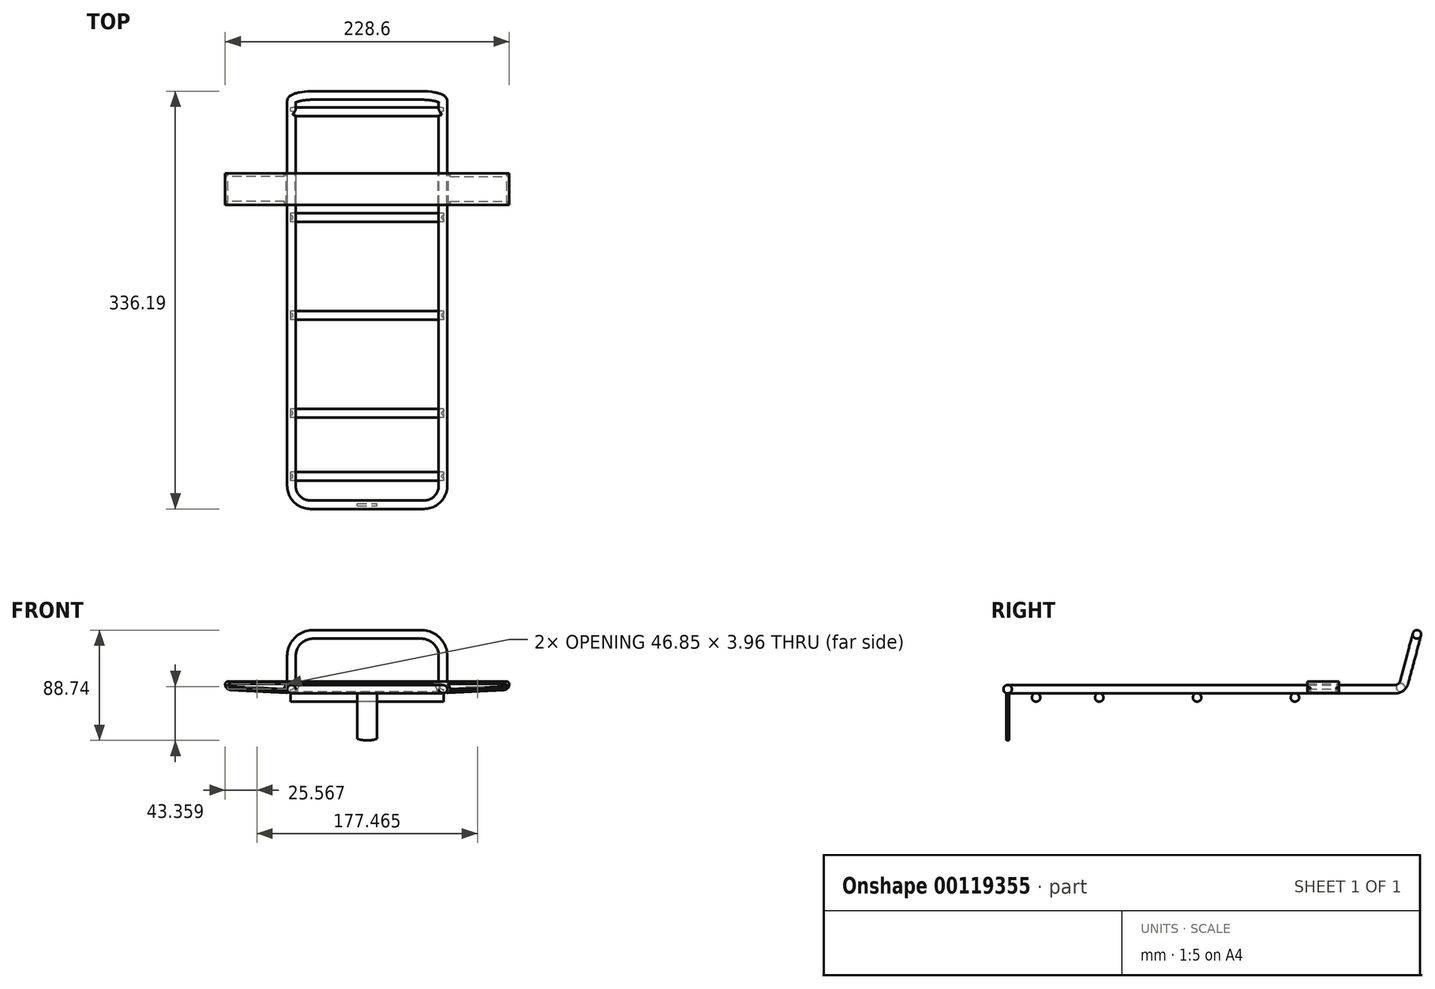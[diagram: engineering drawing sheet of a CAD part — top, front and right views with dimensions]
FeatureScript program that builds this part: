
annotation { "Feature Type Name" : "Feature", "Feature Type Description" : "" }
export const myFeature = defineFeature(function(context is Context, id is Id, definition is map)
    precondition{}
    {
        {
            var Q0;
            Q0=qCreatedBy(makeId("Right.planeOp"),FACE);
            var sketch = newSketch(context, id + "F0", { "sketchPlane" : qUnion([Q0])});
            skCircle(sketch, "E0", {"center": v(0, 0) * mm, "radius": 3.43 * mm});
            skSolve(sketch);
        }
        {
            var Q0;
            Q0=qCreatedBy(makeId("Top.planeOp"),FACE);
            var sketch = newSketch(context, id + "F1", { "sketchPlane" : qUnion([Q0])});
            skLineSegment(sketch, "E1", {"start": v(0, 0) * mm, "end": v(45.72, 0) * mm});
            skArc(sketch, "E2", {"start": v(45.72, 0) * mm, "mid": v(56.5, 4.46) * mm, "end": v(60.96, 15.24) * mm});
            skLineSegment(sketch, "E3", {"start": v(45.72, 0) * mm, "end": v(60.96, 0) * mm, "construction": true});
            skLineSegment(sketch, "E4", {"start": v(60.96, 0) * mm, "end": v(60.96, 15.24) * mm, "construction": true});
            skSolve(sketch);
        }
        {
            var Q0;
            Q0=sQuery(id+"F1.wireOp",EDGE,"E4");
            cPlane(context, id + "F2", {"entities" : qUnion([Q0]), "cplaneType" : CPlaneType.LINE_ANGLE, "offset" : 25.4 * mm, "angle" : 90 * degree, "width" : 152.4 * mm, "height" : 152.4 * mm});
        }
        {
            var Q0;
            Q0=qCreatedBy(id+"F2.planeOp",FACE);
            var sketch = newSketch(context, id + "F3", { "sketchPlane" : qUnion([Q0])});
            skLineSegment(sketch, "E5", {"start": v(15.24, 0) * mm, "end": v(311.65, 0) * mm});
            skArc(sketch, "E6", {"start": v(311.65, 0) * mm, "mid": v(316.3, 1.57) * mm, "end": v(319.01, 5.65) * mm});
            skLineSegment(sketch, "E7", {"start": v(311.65, 0) * mm, "end": v(317.5, 0) * mm, "construction": true});
            skLineSegment(sketch, "E8", {"start": v(317.5, 0) * mm, "end": v(319.01, 5.65) * mm, "construction": true});
            skSolve(sketch);
        }
        {
            var Q0;
            Q0=sQuery(id+"F3.wireOp",EDGE,"E8");
            cPlane(context, id + "F4", {"entities" : qUnion([Q0]), "cplaneType" : CPlaneType.LINE_ANGLE, "offset" : 25.4 * mm, "angle" : 90 * degree, "width" : 152.4 * mm, "height" : 152.4 * mm});
        }
        {
            var Q0;
            Q0=qCreatedBy(id+"F4.planeOp",FACE);
            var sketch = newSketch(context, id + "F5", { "sketchPlane" : qUnion([Q0])});
            skLineSegment(sketch, "E9", {"start": v(-60.96, 88.02) * mm, "end": v(-60.96, 110.12) * mm});
            skArc(sketch, "E10", {"start": v(-43.18, 127.9) * mm, "mid": v(-55.75, 122.69) * mm, "end": v(-60.96, 110.12) * mm});
            skLineSegment(sketch, "E11", {"start": v(-43.18, 127.9) * mm, "end": v(43.18, 127.9) * mm});
            skArc(sketch, "E12", {"start": v(60.96, 110.12) * mm, "mid": v(55.75, 122.69) * mm, "end": v(43.18, 127.9) * mm});
            skLineSegment(sketch, "E13", {"start": v(60.96, 110.12) * mm, "end": v(60.96, 88.02) * mm});
            skLineSegment(sketch, "E14", {"start": v(-60.96, 110.12) * mm, "end": v(-60.96, 127.9) * mm, "construction": true});
            skLineSegment(sketch, "E15", {"start": v(-60.96, 127.9) * mm, "end": v(-43.18, 127.9) * mm, "construction": true});
            skLineSegment(sketch, "E16", {"start": v(43.18, 127.9) * mm, "end": v(60.96, 127.9) * mm, "construction": true});
            skLineSegment(sketch, "E17", {"start": v(60.96, 127.9) * mm, "end": v(60.96, 110.12) * mm, "construction": true});
            skLineSegment(sketch, "E18", {"start": v(-60.96, 88.02) * mm, "end": v(60.96, 88.02) * mm, "construction": true});
            skLineSegment(sketch, "E19", {"start": v(0, 88.02) * mm, "end": v(0, 0) * mm, "construction": true});
            skSolve(sketch);
        }
        {
            var Q0;
            Q0=sQuery(id+"F5.wireOp",EDGE,"E13");
            cPlane(context, id + "F6", {"entities" : qUnion([Q0]), "cplaneType" : CPlaneType.LINE_ANGLE, "offset" : 25.4 * mm, "angle" : 0 * degree, "width" : 152.4 * mm, "height" : 152.4 * mm});
        }
        {
            var Q0;
            Q0=qCreatedBy(id+"F6.planeOp",FACE);
            var sketch = newSketch(context, id + "F7", { "sketchPlane" : qUnion([Q0])});
            skArc(sketch, "E20", {"start": v(-319.01, 5.65) * mm, "mid": v(-316.3, 1.57) * mm, "end": v(-311.65, 0) * mm});
            skLineSegment(sketch, "E21", {"start": v(-311.65, 0) * mm, "end": v(-15.24, 0) * mm});
            skSolve(sketch);
        }
        {
            var Q0;
            Q0=qCreatedBy(makeId("Top.planeOp"),FACE);
            var sketch = newSketch(context, id + "F8", { "sketchPlane" : qUnion([Q0])});
            skArc(sketch, "E22", {"start": v(-60.96, 15.24) * mm, "mid": v(-56.5, 4.46) * mm, "end": v(-45.72, 0) * mm});
            skLineSegment(sketch, "E23", {"start": v(-45.72, 0) * mm, "end": v(0, 0) * mm});
            skSolve(sketch);
        }
        {
            var Q0;
            Q0=qSketchRegion(id+"F0",true);
            var Q1;
            Q1=qConstructionFilter(qBodyType(qCreatedBy(id+"F1",EDGE),BodyType.WIRE),ConstructionObject.NO);
            var Q2;
            Q2=qConstructionFilter(qBodyType(qCreatedBy(id+"F3",EDGE),BodyType.WIRE),ConstructionObject.NO);
            var Q3;
            Q3=qConstructionFilter(qBodyType(qCreatedBy(id+"F5",EDGE),BodyType.WIRE),ConstructionObject.NO);
            var Q4;
            Q4=qConstructionFilter(qBodyType(qCreatedBy(id+"F7",EDGE),BodyType.WIRE),ConstructionObject.NO);
            var Q5;
            Q5=qConstructionFilter(qBodyType(qCreatedBy(id+"F8",EDGE),BodyType.WIRE),ConstructionObject.NO);
            sweep(context, id + "F9", {"profiles" : qUnion([Q0]), "path" : qUnion([Q1, Q2, Q3, Q4, Q5])});
        }
        {
            var Q0;
            Q0=qCreatedBy(makeId("Front.planeOp"),FACE);
            var sketch = newSketch(context, id + "F10", { "sketchPlane" : qUnion([Q0])});
            skLineSegment(sketch, "E24.bottom", {"start": v(-8, 0) * mm, "end": v(8, 0) * mm});
            skLineSegment(sketch, "E24.left", {"start": v(-8, 0) * mm, "end": v(-8, -39.85) * mm});
            skLineSegment(sketch, "E24.right", {"start": v(8, 0) * mm, "end": v(8, -39.85) * mm});
            skArc(sketch, "E25", {"start": v(-8, -39.85) * mm, "mid": v(0, -41.15) * mm, "end": v(8, -39.85) * mm});
            skSolve(sketch);
        }
        {
            var Q0;
            Q0=qSketchRegion(id+"F10",true);
            extrude(context, id + "F11", {"entities" : qUnion([Q0]), "operationType" : NewBodyOperationType.ADD, "endBound" : BoundingType.SYMMETRIC, "depth" : 2.03 * mm});
        }
        {
            var Q0;
            Q0=qCreatedBy(makeId("Right.planeOp"),FACE);
            var sketch = newSketch(context, id + "F12", { "sketchPlane" : qUnion([Q0])});
            skCircle(sketch, "E26", {"center": v(22.86, -6.6) * mm, "radius": 3.43 * mm});
            skCircle(sketch, "E27", {"center": v(73.66, -6.6) * mm, "radius": 3.43 * mm});
            skLineSegment(sketch, "E28", {"start": v(0, -3.18) * mm, "end": v(311.65, -3.18) * mm, "construction": true});
            skCircle(sketch, "E29", {"center": v(152.4, -6.6) * mm, "radius": 3.43 * mm});
            skCircle(sketch, "E30", {"center": v(231.14, -6.6) * mm, "radius": 3.43 * mm});
            skCircle(sketch, "E31", {"center": v(316.23, 1.27) * mm, "radius": 3.43 * mm});
            skSolve(sketch);
        }
        {
            var Q0;
            Q0=qSketchRegion(id+"F12",true);
            extrude(context, id + "F13", {"entities" : qUnion([Q0]), "operationType" : NewBodyOperationType.ADD, "endBound" : BoundingType.SYMMETRIC, "depth" : 123.19 * mm});
        }
        {
            var Q0;
            Q0=qCreatedBy(makeId("Front.planeOp"),FACE);
            cPlane(context, id + "F14", {"entities" : qUnion([Q0]), "cplaneType" : CPlaneType.OFFSET, "offset" : 266.7 * mm, "oppositeDirection" : true, "width" : 152.4 * mm, "height" : 152.4 * mm});
        }
        {
            var Q0;
            Q0=qCreatedBy(id+"F14.planeOp",FACE);
            var sketch = newSketch(context, id + "F15", { "sketchPlane" : qUnion([Q0])});
            skCircle(sketch, "E32", {"center": v(-60.96, 0) * mm, "radius": 3.43 * mm, "construction": true});
            skCircle(sketch, "E33", {"center": v(60.96, 0) * mm, "radius": 3.43 * mm, "construction": true});
            skLineSegment(sketch, "E34", {"start": v(60.96, 3.43) * mm, "end": v(-60.96, 3.43) * mm, "construction": true});
            skArc(sketch, "E35", {"start": v(112.01, 6.22) * mm, "mid": v(113.63, 5.55) * mm, "end": v(114.3, 3.94) * mm});
            skArc(sketch, "E36", {"start": v(114.3, 3.94) * mm, "mid": v(113.04, 0.79) * mm, "end": v(109.96, -0.63) * mm});
            skArc(sketch, "E37", {"start": v(-112.01, 6.22) * mm, "mid": v(-113.63, 5.55) * mm, "end": v(-114.3, 3.94) * mm});
            skArc(sketch, "E38", {"start": v(-114.3, 3.94) * mm, "mid": v(-113.04, 0.79) * mm, "end": v(-109.96, -0.63) * mm});
            skArc(sketch, "E39", {"start": v(64.2, -2.2) * mm, "mid": v(60.96, 3.43) * mm, "end": v(57.72, -2.2) * mm});
            skArc(sketch, "E40", {"start": v(64.2, -2.2) * mm, "mid": v(64.2, -2.71) * mm, "end": v(64.67, -2.95) * mm});
            skArc(sketch, "E41", {"start": v(57.72, -2.2) * mm, "mid": v(57.54, -2.88) * mm, "end": v(56.85, -2.73) * mm});
            skArc(sketch, "E42", {"start": v(-57.72, -2.2) * mm, "mid": v(-60.96, 3.43) * mm, "end": v(-64.2, -2.2) * mm});
            skArc(sketch, "E43", {"start": v(-57.72, -2.2) * mm, "mid": v(-57.54, -2.88) * mm, "end": v(-56.85, -2.73) * mm});
            skLineSegment(sketch, "E44", {"start": v(-109.96, -0.63) * mm, "end": v(-64.67, -2.95) * mm});
            skArc(sketch, "E45", {"start": v(-64.2, -2.2) * mm, "mid": v(-64.2, -2.71) * mm, "end": v(-64.67, -2.95) * mm});
            skLineSegment(sketch, "E46", {"start": v(64.67, -2.95) * mm, "end": v(109.96, -0.63) * mm});
            skLineSegment(sketch, "E47", {"start": v(112.01, 6.22) * mm, "end": v(0, 6.22) * mm});
            skLineSegment(sketch, "E48", {"start": v(0, 6.22) * mm, "end": v(-112.01, 6.22) * mm});
            skLineSegment(sketch, "E49", {"start": v(50.99, 4.2) * mm, "end": v(-50.99, 4.2) * mm});
            skArc(sketch, "E50", {"start": v(-56.85, -2.73) * mm, "mid": v(-56.3, -1.63) * mm, "end": v(-56.05, -0.44) * mm});
            skArc(sketch, "E51", {"start": v(56.05, -0.44) * mm, "mid": v(56.3, -1.63) * mm, "end": v(56.85, -2.73) * mm});
            skArc(sketch, "E52", {"start": v(56.05, -0.44) * mm, "mid": v(54.42, 2.86) * mm, "end": v(50.99, 4.2) * mm});
            skArc(sketch, "E53", {"start": v(-50.99, 4.2) * mm, "mid": v(-54.42, 2.86) * mm, "end": v(-56.05, -0.44) * mm});
            skLineSegment(sketch, "E54", {"start": v(64.64, -2.45) * mm, "end": v(57.28, -2.45) * mm, "construction": true});
            skLineSegment(sketch, "E55", {"start": v(-57.28, -2.45) * mm, "end": v(-64.64, -2.45) * mm, "construction": true});
            skSolve(sketch);
        }
        {
            var Q0;
            Q0=qSketchRegion(id+"F15",true);
            extrude(context, id + "F16", {"entities" : qUnion([Q0]), "depth" : 25.4 * mm});
        }
        {
            var Q0;
            Q0=makeQuery(id+"F16.opExtrude","CAP_FACE",FACE,{"disambiguationData":[OSD([sQuery(id+"F15.wireOp",EDGE,"E35"),sQuery(id+"F15.wireOp",EDGE,"E36"),sQuery(id+"F15.wireOp",EDGE,"E37"),sQuery(id+"F15.wireOp",EDGE,"E38"),sQuery(id+"F15.wireOp",EDGE,"E39"),sQuery(id+"F15.wireOp",EDGE,"E40"),sQuery(id+"F15.wireOp",EDGE,"E41"),sQuery(id+"F15.wireOp",EDGE,"E42"),sQuery(id+"F15.wireOp",EDGE,"E43"),sQuery(id+"F15.wireOp",EDGE,"E44"),sQuery(id+"F15.wireOp",EDGE,"E45"),sQuery(id+"F15.wireOp",EDGE,"E46"),sQuery(id+"F15.wireOp",EDGE,"E47"),sQuery(id+"F15.wireOp",EDGE,"E48"),sQuery(id+"F15.wireOp",EDGE,"E49"),sQuery(id+"F15.wireOp",EDGE,"E50"),sQuery(id+"F15.wireOp",EDGE,"E51"),sQuery(id+"F15.wireOp",EDGE,"E52"),sQuery(id+"F15.wireOp",EDGE,"E53")])],"isStart":true});
            var sketch = newSketch(context, id + "F17", { "sketchPlane" : qUnion([Q0])});
            skLineSegment(sketch, "E56", {"start": v(64.57, 4.2) * mm, "end": v(111.31, 4.2) * mm});
            skLineSegment(sketch, "E57", {"start": v(66.72, 0.2) * mm, "end": v(111.35, 2.5) * mm});
            skArc(sketch, "E58", {"start": v(111.31, 4.2) * mm, "mid": v(112.16, 3.36) * mm, "end": v(111.35, 2.5) * mm});
            skArc(sketch, "E59", {"start": v(66.72, 0.2) * mm, "mid": v(66.05, 2.42) * mm, "end": v(64.57, 4.2) * mm});
            skLineSegment(sketch, "E60", {"start": v(-111.31, 4.2) * mm, "end": v(-64.57, 4.2) * mm});
            skLineSegment(sketch, "E61", {"start": v(-66.72, 0.2) * mm, "end": v(-111.35, 2.5) * mm});
            skArc(sketch, "E62", {"start": v(-111.31, 4.2) * mm, "mid": v(-112.16, 3.36) * mm, "end": v(-111.35, 2.5) * mm});
            skArc(sketch, "E63", {"start": v(-64.57, 4.2) * mm, "mid": v(-66.05, 2.42) * mm, "end": v(-66.72, 0.2) * mm});
            skSolve(sketch);
        }
        {
            var Q0;
            Q0=qSketchRegion(id+"F17",true);
            extrude(context, id + "F18", {"entities" : qUnion([Q0]), "operationType" : NewBodyOperationType.REMOVE, "endBound" : BoundingType.UP_TO_NEXT, "oppositeDirection" : true, "depth" : 25.4 * mm});
        }
        {
            var Q0;
            Q0=makeQuery(id+"F16.opExtrude","SWEPT_EDGE",EDGE,{"disambiguationData":[OSD([sQuery(id+"F15.wireOp",EDGE,"E36"),sQuery(id+"F15.wireOp",EDGE,"E46")])]});
            var Q1;
            Q1=makeQuery(id+"F16.opExtrude","SWEPT_FACE",FACE,{"disambiguationData":[OSD([sQuery(id+"F15.wireOp",EDGE,"E46")])]});
            cPlane(context, id + "F19", {"entities" : qUnion([Q0, Q1]), "cplaneType" : CPlaneType.LINE_ANGLE, "offset" : 25.4 * mm, "angle" : 90 * degree, "width" : 152.4 * mm, "height" : 152.4 * mm});
        }
        {
            var Q0;
            Q0=qCreatedBy(id+"F19.planeOp",FACE);
            var sketch = newSketch(context, id + "F20", { "sketchPlane" : qUnion([Q0])});
            skLineSegment(sketch, "E64", {"start": v(241.3, -5.45) * mm, "end": v(241.3, -4.03) * mm});
            skLineSegment(sketch, "E65", {"start": v(241.3, -4.03) * mm, "end": v(243.95, -4.74) * mm});
            skLineSegment(sketch, "E66", {"start": v(243.95, -4.74) * mm, "end": v(241.3, -5.45) * mm});
            skLineSegment(sketch, "E67", {"start": v(241.3, -6.27) * mm, "end": v(241.3, -5.45) * mm, "construction": true});
            skLineSegment(sketch, "E68", {"start": v(266.7, -6.27) * mm, "end": v(266.7, -5.45) * mm, "construction": true});
            skLineSegment(sketch, "E69", {"start": v(266.7, -5.45) * mm, "end": v(266.7, -4.03) * mm});
            skLineSegment(sketch, "E70", {"start": v(266.7, -4.03) * mm, "end": v(264.05, -4.74) * mm});
            skLineSegment(sketch, "E71", {"start": v(264.05, -4.74) * mm, "end": v(266.7, -5.45) * mm});
            skSolve(sketch);
        }
        {
            var Q0;
            Q0=qSketchRegion(id+"F20",true);
            var Q1;
            Q1=makeQuery(id+"F18.boolean.opBoolean","COPY",FACE,{"derivedFrom":makeQuery(id+"F18.opExtrude","SWEPT_FACE",FACE,{"disambiguationData":[OSD([sQuery(id+"F17.wireOp",EDGE,"E63")])]})});
            var Q2;
            Q2=makeQuery(id+"F16.opExtrude","SWEPT_FACE",FACE,{"disambiguationData":[OSD([sQuery(id+"F15.wireOp",EDGE,"E36")])]});
            extrude(context, id + "F21", {"entities" : qUnion([Q0]), "operationType" : NewBodyOperationType.REMOVE, "endBound" : BoundingType.UP_TO_SURFACE, "oppositeDirection" : true, "endBoundEntityFace" : qUnion([Q1]), "depth" : 152.4 * mm, "hasSecondDirection" : true, "secondDirectionBound" : SecondDirectionBoundingType.UP_TO_SURFACE, "secondDirectionOppositeDirection" : false, "secondDirectionBoundEntityFace" : qUnion([Q2]), "secondDirectionDepth" : 25.4 * mm});
        }
        {
            var Q0;
            Q0=makeQuery(id+"F16.opExtrude","SWEPT_EDGE",EDGE,{"disambiguationData":[OSD([sQuery(id+"F15.wireOp",EDGE,"E38"),sQuery(id+"F15.wireOp",EDGE,"E44")])]});
            var Q1;
            Q1=makeQuery(id+"F16.opExtrude","SWEPT_FACE",FACE,{"disambiguationData":[OSD([sQuery(id+"F15.wireOp",EDGE,"E44")])]});
            cPlane(context, id + "F22", {"entities" : qUnion([Q0, Q1]), "cplaneType" : CPlaneType.LINE_ANGLE, "offset" : 25.4 * mm, "angle" : 90 * degree, "width" : 152.4 * mm, "height" : 152.4 * mm});
        }
        {
            var Q0;
            Q0=qCreatedBy(id+"F22.planeOp",FACE);
            var sketch = newSketch(context, id + "F23", { "sketchPlane" : qUnion([Q0])});
            skLineSegment(sketch, "E72", {"start": v(266.7, -4.03) * mm, "end": v(264.05, -4.74) * mm});
            skLineSegment(sketch, "E73", {"start": v(266.7, -4.03) * mm, "end": v(266.7, -5.45) * mm});
            skLineSegment(sketch, "E74", {"start": v(266.7, -5.45) * mm, "end": v(264.05, -4.74) * mm});
            skLineSegment(sketch, "E75", {"start": v(266.7, -5.45) * mm, "end": v(266.7, -6.27) * mm, "construction": true});
            skLineSegment(sketch, "E76", {"start": v(241.3, -6.27) * mm, "end": v(241.3, -5.45) * mm, "construction": true});
            skLineSegment(sketch, "E77", {"start": v(241.3, -5.45) * mm, "end": v(241.3, -4.03) * mm});
            skLineSegment(sketch, "E78", {"start": v(241.3, -4.03) * mm, "end": v(243.95, -4.74) * mm});
            skLineSegment(sketch, "E79", {"start": v(243.95, -4.74) * mm, "end": v(241.3, -5.45) * mm});
            skSolve(sketch);
        }
        {
            var Q0;
            Q0=qSketchRegion(id+"F23",true);
            var Q1;
            Q1=makeQuery(id+"F18.boolean.opBoolean","COPY",FACE,{"derivedFrom":makeQuery(id+"F18.opExtrude","SWEPT_FACE",FACE,{"disambiguationData":[OSD([sQuery(id+"F17.wireOp",EDGE,"E59")])]})});
            var Q2;
            Q2=makeQuery(id+"F16.opExtrude","SWEPT_FACE",FACE,{"disambiguationData":[OSD([sQuery(id+"F15.wireOp",EDGE,"E38")])]});
            extrude(context, id + "F24", {"entities" : qUnion([Q0]), "operationType" : NewBodyOperationType.REMOVE, "endBound" : BoundingType.UP_TO_SURFACE, "endBoundEntityFace" : qUnion([Q1]), "depth" : 152.4 * mm, "hasSecondDirection" : true, "secondDirectionBound" : SecondDirectionBoundingType.UP_TO_SURFACE, "secondDirectionOppositeDirection" : true, "secondDirectionBoundEntityFace" : qUnion([Q2]), "secondDirectionDepth" : 25.4 * mm});
        }
        {
            var Q0;
            Q0=qCreatedBy(id+"F19.planeOp",FACE);
            var sketch = newSketch(context, id + "F25", { "sketchPlane" : qUnion([Q0])});
            skLineSegment(sketch, "E80", {"start": v(239.52, -3.63) * mm, "end": v(243.66, -4.74) * mm});
            skLineSegment(sketch, "E81", {"start": v(243.66, -4.74) * mm, "end": v(240.8, -5.51) * mm});
            skLineSegment(sketch, "E82", {"start": v(240.8, -5.51) * mm, "end": v(240.8, -9.32) * mm});
            skLineSegment(sketch, "E83", {"start": v(267.2, -9.32) * mm, "end": v(267.2, -5.51) * mm});
            skLineSegment(sketch, "E84", {"start": v(267.2, -5.51) * mm, "end": v(264.34, -4.74) * mm});
            skLineSegment(sketch, "E85", {"start": v(264.34, -4.74) * mm, "end": v(268.48, -3.63) * mm});
            skLineSegment(sketch, "E86", {"start": v(268.48, -3.63) * mm, "end": v(268.48, -10.59) * mm});
            skLineSegment(sketch, "E87", {"start": v(268.48, -10.59) * mm, "end": v(239.52, -10.59) * mm});
            skLineSegment(sketch, "E88", {"start": v(239.52, -10.59) * mm, "end": v(239.52, -3.63) * mm});
            skLineSegment(sketch, "E89.top", {"start": v(240.8, -9.32) * mm, "end": v(267.2, -9.32) * mm});
            skLineSegment(sketch, "E90", {"start": v(254, -9.32) * mm, "end": v(254, -10.59) * mm, "construction": true});
            skLineSegment(sketch, "E91", {"start": v(266.7, -5.86) * mm, "end": v(267.2, -5.86) * mm, "construction": true});
            skLineSegment(sketch, "E92", {"start": v(240.8, -5.86) * mm, "end": v(241.3, -5.86) * mm, "construction": true});
            skLineSegment(sketch, "E93", {"start": v(267.2, -7.41) * mm, "end": v(268.48, -7.41) * mm, "construction": true});
            skLineSegment(sketch, "E94", {"start": v(241.6, -4.19) * mm, "end": v(241.61, -4.12) * mm, "construction": true});
            skLineSegment(sketch, "E95", {"start": v(242.23, -5.13) * mm, "end": v(242.25, -5.2) * mm, "construction": true});
            skLineSegment(sketch, "E96", {"start": v(265.77, -5.13) * mm, "end": v(265.75, -5.2) * mm, "construction": true});
            skLineSegment(sketch, "E97", {"start": v(266.4, -4.19) * mm, "end": v(266.39, -4.12) * mm, "construction": true});
            skSolve(sketch);
        }
        {
            var Q0;
            Q0=qSketchRegion(id+"F25",true);
            extrude(context, id + "F26", {"entities" : qUnion([Q0]), "oppositeDirection" : true, "depth" : 25.4 * mm});
        }
        {
            var Q0;
            Q0=makeQuery(id+"F26.opExtrude","SWEPT_EDGE",EDGE,{"disambiguationData":[OSD([sQuery(id+"F25.wireOp",EDGE,"E80"),sQuery(id+"F25.wireOp",EDGE,"E81")])]});
            var Q1;
            Q1=makeQuery(id+"F26.opExtrude","SWEPT_EDGE",EDGE,{"disambiguationData":[OSD([sQuery(id+"F25.wireOp",EDGE,"E84"),sQuery(id+"F25.wireOp",EDGE,"E85")])]});
            fillet(context, id + "F27", {"entities" : qUnion([Q0, Q1]), "radius" : 0.4 * mm, "tangentPropagation" : true, "allowEdgeOverflow" : false});
        }
        {
            var Q0;
            Q0=makeQuery(id+"F26.opExtrude","SWEPT_EDGE",EDGE,{"disambiguationData":[OSD([sQuery(id+"F25.wireOp",EDGE,"E81"),sQuery(id+"F25.wireOp",EDGE,"E82")])]});
            var Q1;
            Q1=makeQuery(id+"F26.opExtrude","SWEPT_EDGE",EDGE,{"disambiguationData":[OSD([sQuery(id+"F25.wireOp",EDGE,"E82"),sQuery(id+"F25.wireOp",EDGE,"E89.top")])]});
            var Q2;
            Q2=makeQuery(id+"F26.opExtrude","SWEPT_EDGE",EDGE,{"disambiguationData":[OSD([sQuery(id+"F25.wireOp",EDGE,"E83"),sQuery(id+"F25.wireOp",EDGE,"E89.top")])]});
            var Q3;
            Q3=makeQuery(id+"F26.opExtrude","SWEPT_EDGE",EDGE,{"disambiguationData":[OSD([sQuery(id+"F25.wireOp",EDGE,"E83"),sQuery(id+"F25.wireOp",EDGE,"E84")])]});
            fillet(context, id + "F28", {"entities" : qUnion([Q0, Q1, Q2, Q3]), "radius" : 0.5 * mm, "tangentPropagation" : true, "allowEdgeOverflow" : false});
        }
        {
            var Q0;
            Q0=makeQuery(id+"F26.opExtrude","SWEPT_EDGE",EDGE,{"disambiguationData":[OSD([sQuery(id+"F25.wireOp",EDGE,"E85"),sQuery(id+"F25.wireOp",EDGE,"E86")])]});
            var Q1;
            Q1=makeQuery(id+"F26.opExtrude","SWEPT_EDGE",EDGE,{"disambiguationData":[OSD([sQuery(id+"F25.wireOp",EDGE,"E86"),sQuery(id+"F25.wireOp",EDGE,"E87")])]});
            var Q2;
            Q2=makeQuery(id+"F26.opExtrude","SWEPT_EDGE",EDGE,{"disambiguationData":[OSD([sQuery(id+"F25.wireOp",EDGE,"E87"),sQuery(id+"F25.wireOp",EDGE,"E88")])]});
            var Q3;
            Q3=makeQuery(id+"F26.opExtrude","SWEPT_EDGE",EDGE,{"disambiguationData":[OSD([sQuery(id+"F25.wireOp",EDGE,"E80"),sQuery(id+"F25.wireOp",EDGE,"E88")])]});
            fillet(context, id + "F29", {"entities" : qUnion([Q0, Q1, Q2, Q3]), "radius" : 1.27 * mm, "tangentPropagation" : true, "allowEdgeOverflow" : false});
        }
        {
            var Q0;
            Q0=makeQuery(id+"F18.boolean.opBoolean","COPY",EDGE,{"derivedFrom":makeQuery(id+"F18.opExtrude","SWEPT_EDGE",EDGE,{"disambiguationData":[OSD([sQuery(id+"F17.wireOp",EDGE,"E57"),sQuery(id+"F17.wireOp",EDGE,"E59")])]})});
            var Q1;
            Q1=makeQuery(id+"F18.boolean.opBoolean","COPY",EDGE,{"derivedFrom":makeQuery(id+"F18.opExtrude","SWEPT_EDGE",EDGE,{"disambiguationData":[OSD([sQuery(id+"F17.wireOp",EDGE,"E56"),sQuery(id+"F17.wireOp",EDGE,"E59")])]})});
            var Q2;
            Q2=makeQuery(id+"F18.boolean.opBoolean","COPY",EDGE,{"derivedFrom":makeQuery(id+"F18.opExtrude","SWEPT_EDGE",EDGE,{"disambiguationData":[OSD([sQuery(id+"F17.wireOp",EDGE,"E60"),sQuery(id+"F17.wireOp",EDGE,"E63")])]})});
            var Q3;
            Q3=makeQuery(id+"F18.boolean.opBoolean","COPY",EDGE,{"derivedFrom":makeQuery(id+"F18.opExtrude","SWEPT_EDGE",EDGE,{"disambiguationData":[OSD([sQuery(id+"F17.wireOp",EDGE,"E61"),sQuery(id+"F17.wireOp",EDGE,"E63")])]})});
            fillet(context, id + "F30", {"entities" : qUnion([Q0, Q1, Q2, Q3]), "radius" : 0.5 * mm, "tangentPropagation" : true, "allowEdgeOverflow" : false});
        }
        {
            var Q0;
            Q0=makeQuery(id+"F26.opExtrude","SWEPT_BODY",BODY,{"disambiguationData":[OSD([sQuery(id+"F25.wireOp",EDGE,"E80"),sQuery(id+"F25.wireOp",EDGE,"E81"),sQuery(id+"F25.wireOp",EDGE,"E82"),sQuery(id+"F25.wireOp",EDGE,"E83"),sQuery(id+"F25.wireOp",EDGE,"E84"),sQuery(id+"F25.wireOp",EDGE,"E85"),sQuery(id+"F25.wireOp",EDGE,"E86"),sQuery(id+"F25.wireOp",EDGE,"E87"),sQuery(id+"F25.wireOp",EDGE,"E88"),sQuery(id+"F25.wireOp",EDGE,"E89.top")])]});
            deleteBodies(context, id + "F31", {"entities" : qUnion([Q0])});
        }
    });
